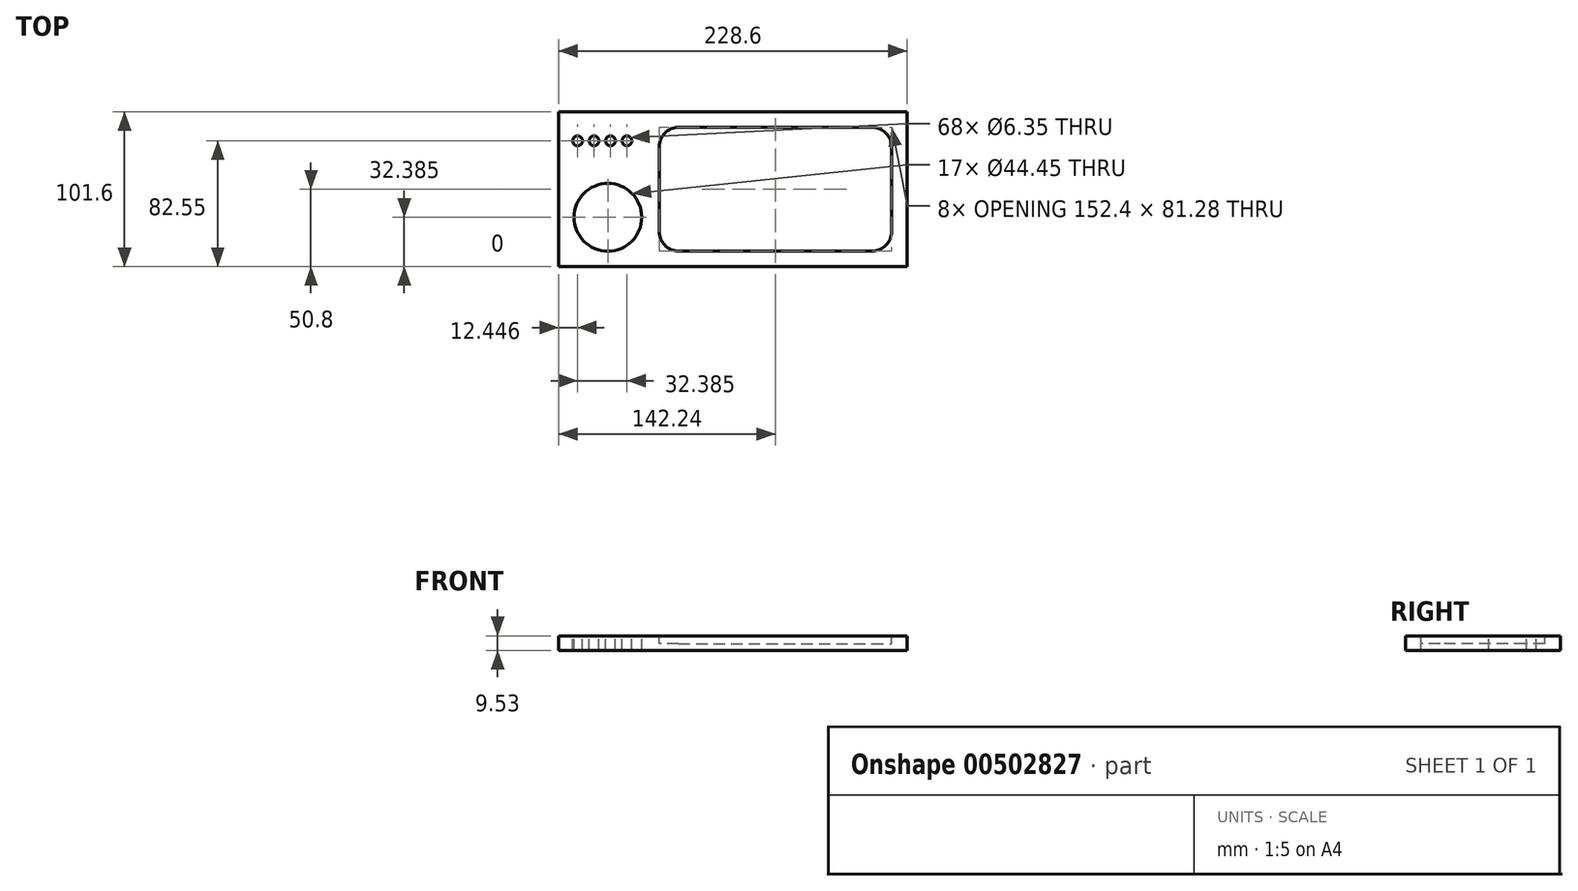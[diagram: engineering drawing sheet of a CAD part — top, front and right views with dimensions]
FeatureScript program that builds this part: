
annotation { "Feature Type Name" : "Feature", "Feature Type Description" : "" }
export const myFeature = defineFeature(function(context is Context, id is Id, definition is map)
    precondition{}
    {
        {
            var Q0;
            Q0=qCreatedBy(makeId("Top.planeOp"),FACE);
            var sketch = newSketch(context, id + "F0", { "sketchPlane" : qUnion([Q0])});
            skLineSegment(sketch, "E0.bottom", {"start": v(0, 0) * mm, "end": v(228.6, 0) * mm});
            skLineSegment(sketch, "E0.top", {"start": v(0, -101.6) * mm, "end": v(228.6, -101.6) * mm});
            skLineSegment(sketch, "E0.left", {"start": v(0, 0) * mm, "end": v(0, -101.6) * mm});
            skLineSegment(sketch, "E0.right", {"start": v(228.6, 0) * mm, "end": v(228.6, -101.6) * mm});
            skCircle(sketch, "E1", {"center": v(32.39, -69.22) * mm, "radius": 22.23 * mm});
            skLineSegment(sketch, "E2.bottom", {"start": v(78.74, -10.16) * mm, "end": v(205.74, -10.16) * mm});
            skLineSegment(sketch, "E2.top", {"start": v(78.74, -91.44) * mm, "end": v(205.74, -91.44) * mm});
            skLineSegment(sketch, "E2.left", {"start": v(66.04, -22.86) * mm, "end": v(66.04, -78.74) * mm});
            skLineSegment(sketch, "E2.right", {"start": v(218.44, -22.86) * mm, "end": v(218.44, -78.74) * mm});
            skCircle(sketch, "E3", {"center": v(12.45, -19.05) * mm, "radius": 3.18 * mm});
            skCircle(sketch, "E4", {"center": v(23.24, -19.05) * mm, "radius": 3.18 * mm});
            skCircle(sketch, "E5", {"center": v(34.04, -19.05) * mm, "radius": 3.18 * mm});
            skCircle(sketch, "E6", {"center": v(44.83, -19.05) * mm, "radius": 3.18 * mm});
            skPoint(sketch, "E7.visualSharp", {"position": v(66.04, -10.16) * mm});
            skArc(sketch, "E7.filletArc", {"start": v(78.74, -10.16) * mm, "mid": v(69.76, -13.88) * mm, "end": v(66.04, -22.86) * mm});
            skPoint(sketch, "E8.visualSharp", {"position": v(66.04, -91.44) * mm});
            skArc(sketch, "E8.filletArc", {"start": v(66.04, -78.74) * mm, "mid": v(69.76, -87.72) * mm, "end": v(78.74, -91.44) * mm});
            skPoint(sketch, "E9.visualSharp", {"position": v(218.44, -10.16) * mm});
            skArc(sketch, "E9.filletArc", {"start": v(218.44, -22.86) * mm, "mid": v(214.72, -13.88) * mm, "end": v(205.74, -10.16) * mm});
            skPoint(sketch, "E10.visualSharp", {"position": v(218.44, -91.44) * mm});
            skArc(sketch, "E10.filletArc", {"start": v(205.74, -91.44) * mm, "mid": v(214.72, -87.72) * mm, "end": v(218.44, -78.74) * mm});
            skSolve(sketch);
        }
        {
            var Q0;
            Q0=makeQuery(id+"F0.imprint","IMPRINT",FACE,{"disambiguationData":[TD([[makeQuery(id+"F0.imprint","IMPRINT",EDGE,{"derivedFrom":sQuery(id+"F0.wireOp",EDGE,"E0.bottom")}),-1.0]])]});
            var Q1;
            Q1=makeQuery(id+"F0.imprint","IMPRINT",FACE,{"disambiguationData":[TD([[makeQuery(id+"F0.imprint","IMPRINT",EDGE,{"derivedFrom":sQuery(id+"F0.wireOp",EDGE,"E2.bottom")}),-1.0]])]});
            extrude(context, id + "F1", {"entities" : qUnion([Q0, Q1]), "oppositeDirection" : true, "depth" : 9.52 * mm, "offsetDistance" : 25.4 * mm});
        }
        {
            var Q0;
            Q0=makeQuery(id+"F0.imprint","IMPRINT",FACE,{"disambiguationData":[TD([[makeQuery(id+"F0.imprint","IMPRINT",EDGE,{"derivedFrom":sQuery(id+"F0.wireOp",EDGE,"E2.bottom")}),-1.0]])]});
            extrude(context, id + "F2", {"entities" : qUnion([Q0]), "operationType" : NewBodyOperationType.REMOVE, "oppositeDirection" : true, "depth" : 5.08 * mm, "offsetDistance" : 25.4 * mm});
        }
    });
